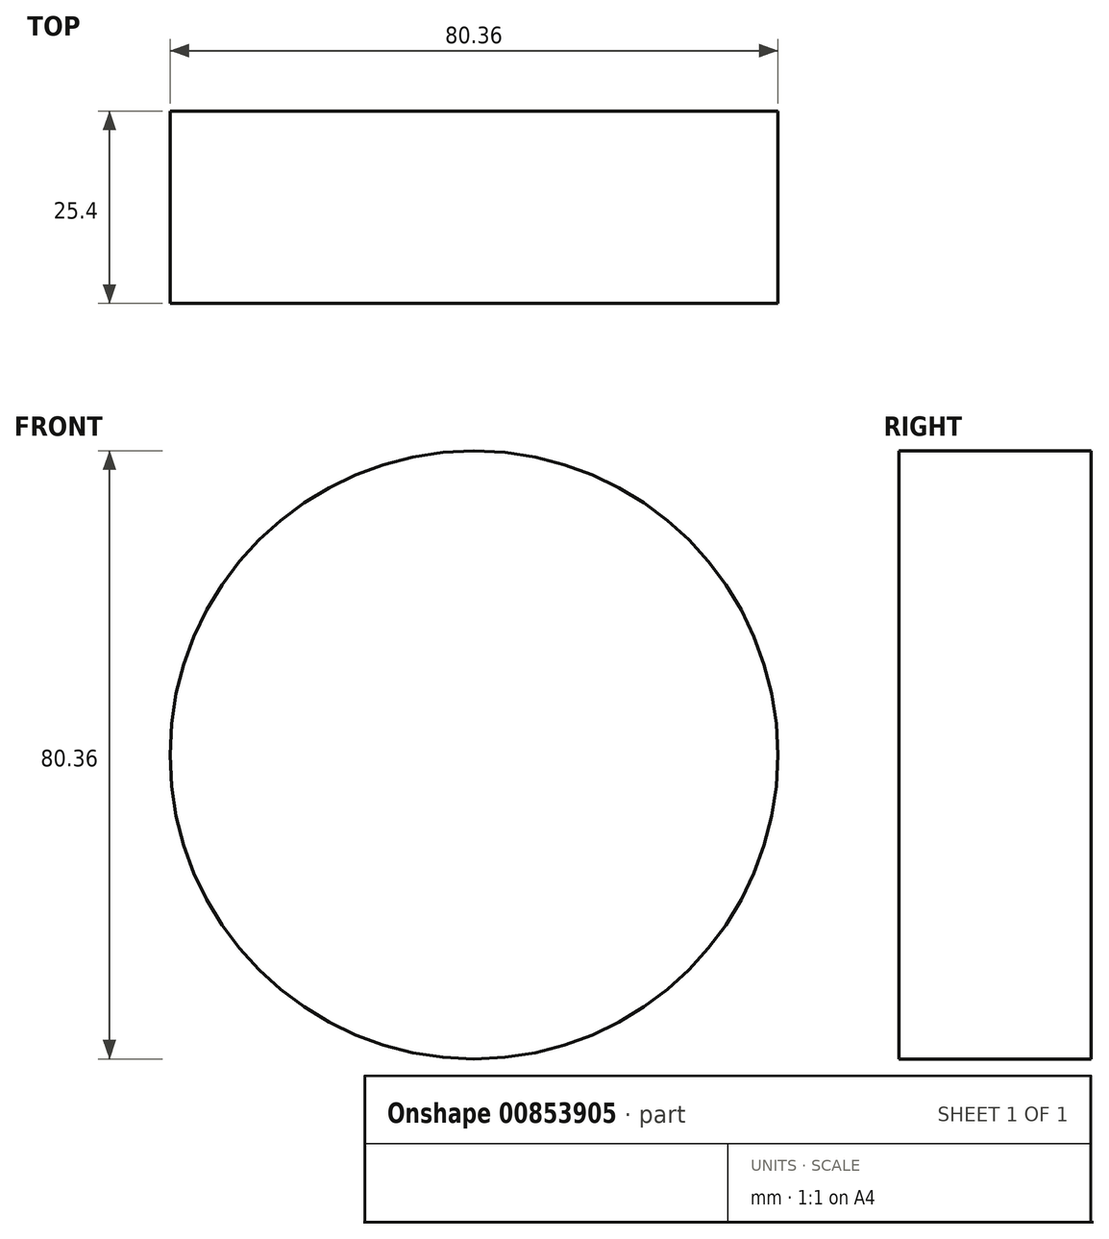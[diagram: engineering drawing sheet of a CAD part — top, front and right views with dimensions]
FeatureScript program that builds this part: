
annotation { "Feature Type Name" : "Feature", "Feature Type Description" : "" }
export const myFeature = defineFeature(function(context is Context, id is Id, definition is map)
    precondition{}
    {
        {
            var Q0;
            Q0=qCreatedBy(makeId("Front.planeOp"),FACE);
            var sketch = newSketch(context, id + "F0", { "sketchPlane" : qUnion([Q0])});
            skCircle(sketch, "E0", {"center": v(0, 0) * mm, "radius": 40.18 * mm});
            skSolve(sketch);
        }
        {
            var Q0;
            Q0=makeQuery(id+"F0.imprint","IMPRINT",FACE,{"disambiguationData":[TD([[makeQuery(id+"F0.imprint","IMPRINT",EDGE,{"derivedFrom":sQuery(id+"F0.wireOp",EDGE,"E0")}),1.0]])]});
            extrude(context, id + "F1", {"entities" : qUnion([Q0]), "depth" : 25.4 * mm, "offsetDistance" : 25.4 * mm});
        }
    });
